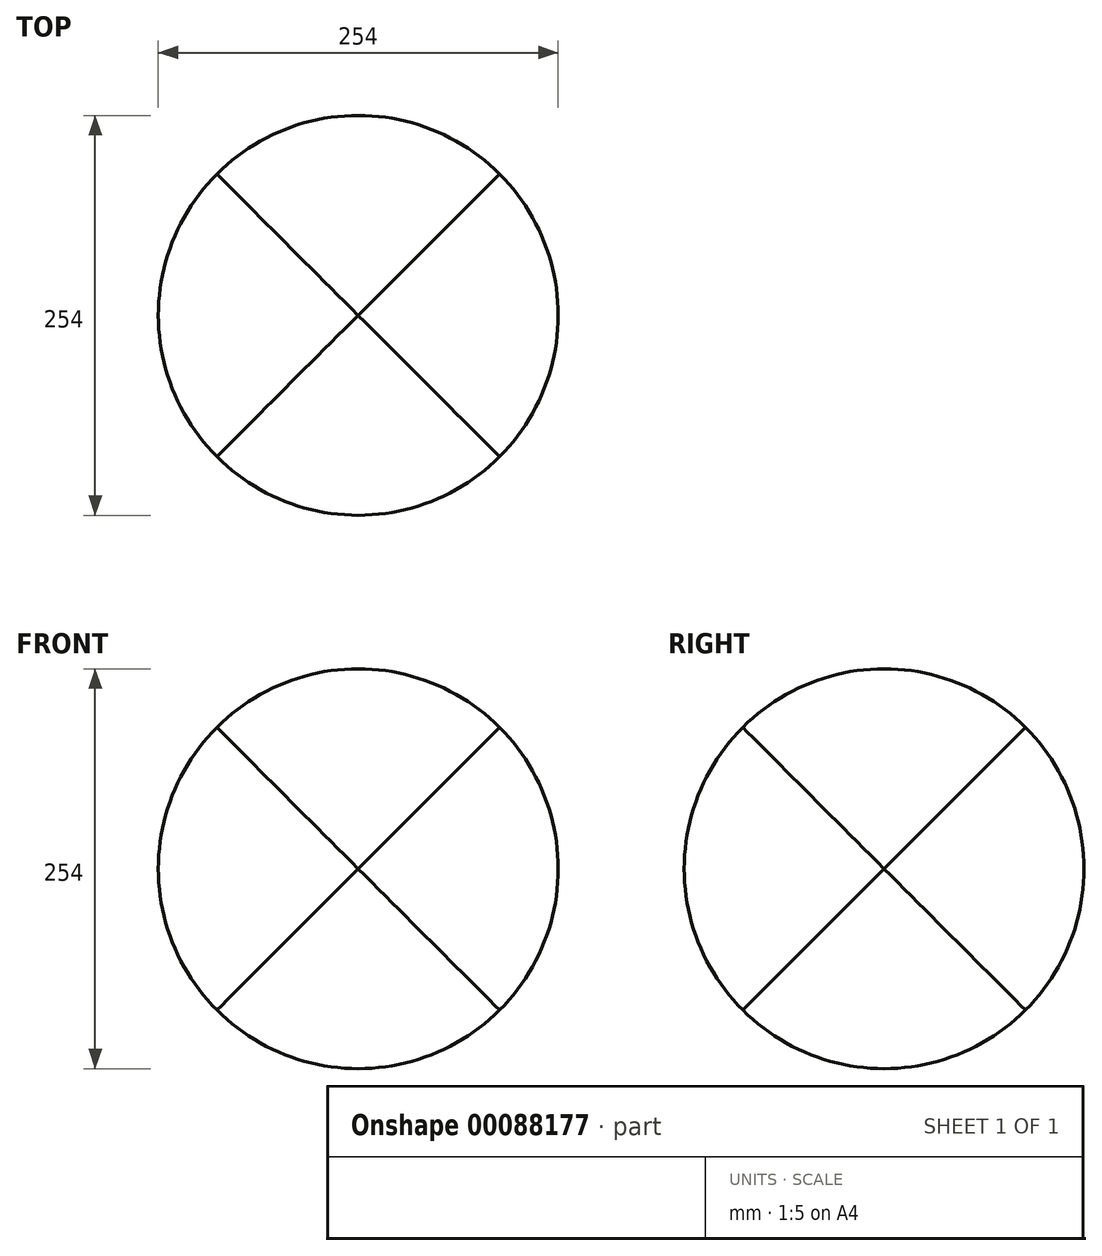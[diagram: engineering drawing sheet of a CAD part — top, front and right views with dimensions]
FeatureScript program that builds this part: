
annotation { "Feature Type Name" : "Feature", "Feature Type Description" : "" }
export const myFeature = defineFeature(function(context is Context, id is Id, definition is map)
    precondition{}
    {
        {
            var Q0;
            Q0=qCreatedBy(makeId("Front.planeOp"),FACE);
            var sketch = newSketch(context, id + "F0", { "sketchPlane" : qUnion([Q0])});
            skCircle(sketch, "E0", {"center": v(0, 0) * mm, "radius": 127 * mm});
            skSolve(sketch);
        }
        {
            var Q0;
            Q0 = qSketchRegion(id + "F0", true);
            extrude(context, id + "F1", {"entities" : qUnion([Q0]), "endBound" : BoundingType.SYMMETRIC, "depth" : 254 * mm});
        }
        {
            var Q0;
            Q0=qCreatedBy(makeId("Right.planeOp"),FACE);
            var sketch = newSketch(context, id + "F2", { "sketchPlane" : qUnion([Q0])});
            skCircle(sketch, "E1", {"center": v(0, 0) * mm, "radius": 127 * mm});
            skSolve(sketch);
        }
        {
            var Q0;
            Q0 = qSketchRegion(id + "F2", true);
            extrude(context, id + "F3", {"entities" : qUnion([Q0]), "operationType" : NewBodyOperationType.INTERSECT, "endBound" : BoundingType.SYMMETRIC, "depth" : 254 * mm});
        }
        {
            var Q0;
            Q0=qCreatedBy(makeId("Top.planeOp"),FACE);
            var sketch = newSketch(context, id + "F4", { "sketchPlane" : qUnion([Q0])});
            skCircle(sketch, "E2", {"center": v(0, 0) * mm, "radius": 127 * mm});
            skSolve(sketch);
        }
        {
            var Q0;
            Q0 = qSketchRegion(id + "F4", true);
            extrude(context, id + "F5", {"entities" : qUnion([Q0]), "operationType" : NewBodyOperationType.INTERSECT, "endBound" : BoundingType.SYMMETRIC, "depth" : 254 * mm});
        }
    });
